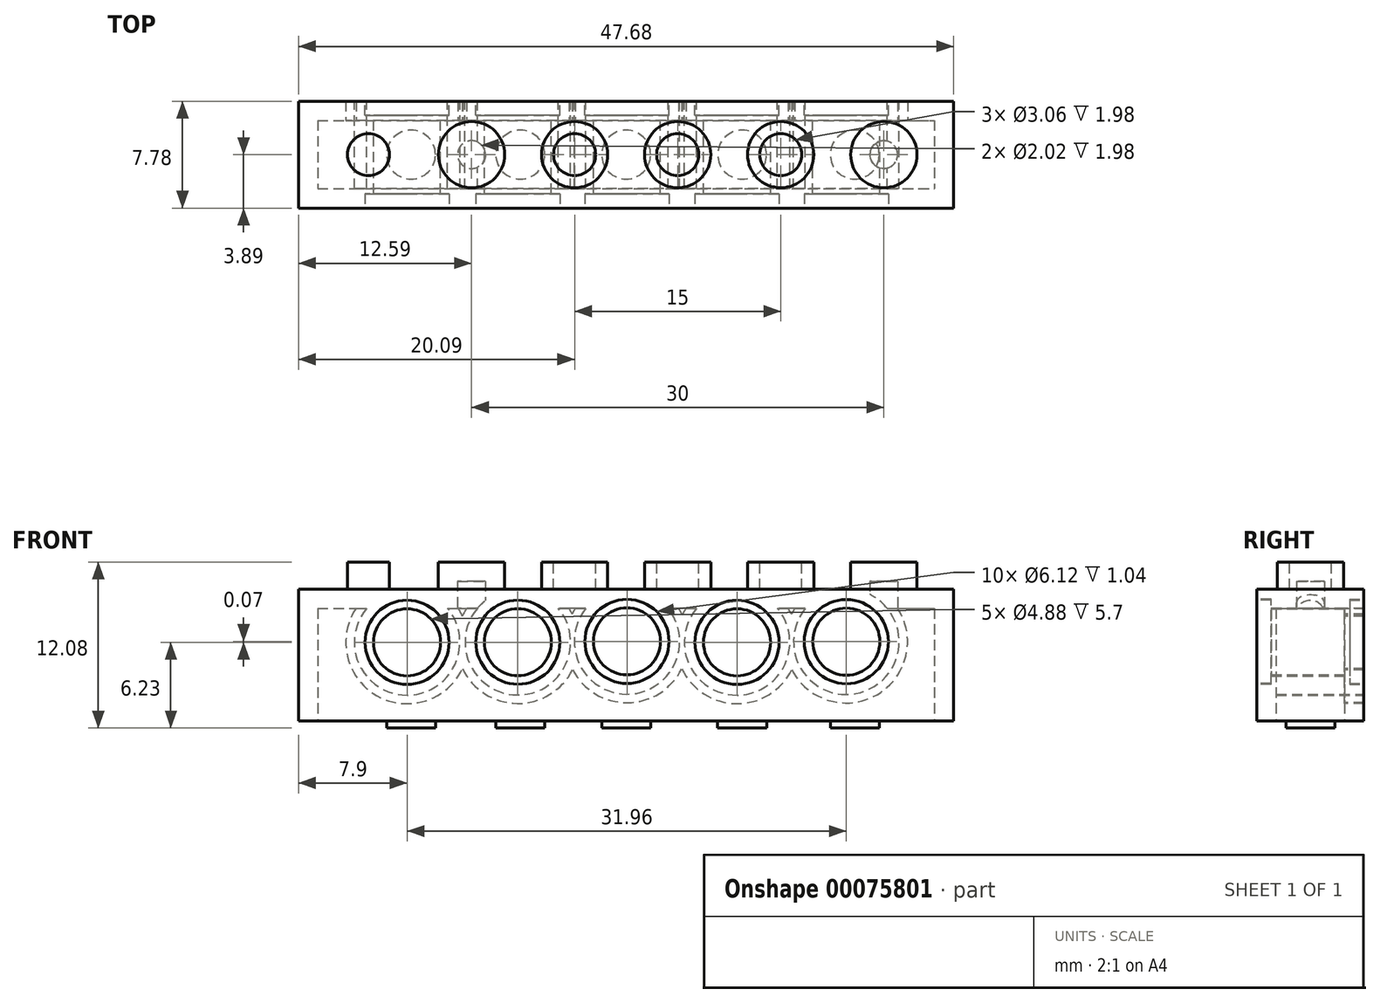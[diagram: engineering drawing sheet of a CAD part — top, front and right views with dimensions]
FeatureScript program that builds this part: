
annotation { "Feature Type Name" : "Feature", "Feature Type Description" : "" }
export const myFeature = defineFeature(function(context is Context, id is Id, definition is map)
    precondition{}
    {
        {
            var Q0;
            Q0=qCreatedBy(makeId("Top.planeOp"),FACE);
            var sketch = newSketch(context, id + "F0", { "sketchPlane" : qUnion([Q0])});
            skLineSegment(sketch, "E0.bottom", {"start": v(-23.84, 3.89) * mm, "end": v(23.84, 3.89) * mm});
            skLineSegment(sketch, "E0.top", {"start": v(-23.84, -3.89) * mm, "end": v(23.84, -3.89) * mm});
            skLineSegment(sketch, "E0.left", {"start": v(-23.84, 3.89) * mm, "end": v(-23.84, -3.89) * mm});
            skLineSegment(sketch, "E0.right", {"start": v(23.84, 3.89) * mm, "end": v(23.84, -3.89) * mm});
            skPoint(sketch, "E0.middle", {"position": v(0, 0) * mm});
            skSolve(sketch);
        }
        {
            var Q0;
            Q0=makeQuery(id+"F0.imprint","IMPRINT",FACE,{"disambiguationData":[TD([[makeQuery(id+"F0.imprint","IMPRINT",EDGE,{"derivedFrom":sQuery(id+"F0.wireOp",EDGE,"E0.bottom")}),-1.0]])]});
            extrude(context, id + "F1", {"entities" : qUnion([Q0]), "depth" : 9.6 * mm});
        }
        {
            var Q0;
            Q0=makeQuery(id+"F1.opExtrude","SWEPT_FACE",FACE,{"disambiguationData":[OSD([sQuery(id+"F0.wireOp",EDGE,"E0.bottom")])]});
            var sketch = newSketch(context, id + "F2", { "sketchPlane" : qUnion([Q0])});
            skLineSegment(sketch, "E1", {"start": v(-23.84, 4.8) * mm, "end": v(-18.45, 4.8) * mm});
            skLineSegment(sketch, "E2", {"start": v(-18.45, 9.6) * mm, "end": v(-18.45, 8.26) * mm});
            skLineSegment(sketch, "E3", {"start": v(-18.45, 0) * mm, "end": v(-18.45, 3.33) * mm});
            skCircle(sketch, "E4", {"center": v(-16.02, 5.78) * mm, "radius": 2.44 * mm});
            skPoint(sketch, "E4.first.point", {"position": v(-18.45, 5.83) * mm});
            skPoint(sketch, "E4.second.point", {"position": v(-13.58, 5.73) * mm});
            skPoint(sketch, "E4.third.point", {"position": v(-16.04, 3.34) * mm});
            skLineSegment(sketch, "E5", {"start": v(-13.58, 5.73) * mm, "end": v(-10.5, 5.73) * mm});
            skCircle(sketch, "E6", {"center": v(-8.07, 5.73) * mm, "radius": 2.44 * mm});
            skPoint(sketch, "E6.second.point", {"position": v(-5.63, 5.73) * mm});
            skPoint(sketch, "E6.third.point", {"position": v(-8.14, 8.17) * mm});
            skLineSegment(sketch, "E7", {"start": v(-5.57, 5.68) * mm, "end": v(-2.5, 5.68) * mm});
            skCircle(sketch, "E8", {"center": v(-0.06, 5.8) * mm, "radius": 2.44 * mm});
            skPoint(sketch, "E8.second.point", {"position": v(2.37, 5.68) * mm});
            skPoint(sketch, "E8.third.point", {"position": v(0, 8.24) * mm});
            skLineSegment(sketch, "E9", {"start": v(2.36, 5.74) * mm, "end": v(5.44, 5.74) * mm});
            skCircle(sketch, "E10", {"center": v(7.88, 5.74) * mm, "radius": 2.44 * mm});
            skPoint(sketch, "E10.second.point", {"position": v(10.31, 5.74) * mm});
            skPoint(sketch, "E10.third.point", {"position": v(7.78, 8.18) * mm});
            skLineSegment(sketch, "E11", {"start": v(10.43, 5.73) * mm, "end": v(13.5, 5.73) * mm});
            skCircle(sketch, "E12", {"center": v(15.94, 5.73) * mm, "radius": 2.44 * mm});
            skPoint(sketch, "E12.second.point", {"position": v(18.38, 5.73) * mm});
            skPoint(sketch, "E12.third.point", {"position": v(15.93, 8.17) * mm});
            skSolve(sketch);
        }
        {
            var Q0;
            Q0=makeQuery(id+"F2.imprint","IMPRINT",FACE,{"disambiguationData":[TD([[makeQuery(id+"F2.imprint","IMPRINT",EDGE,{"derivedFrom":sQuery(id+"F2.wireOp",EDGE,"E6")}),1.0]])]});
            var Q1;
            {var subQ0=sQuery(id+"F2.wireOp",EDGE,"E8");var subQ1=makeQuery(id+"F2.imprint","IMPRINT",VERTEX,{"disambiguationData":[OD(0.0)],"derivedFrom":subQ0});Q1=makeQuery(id+"F2.imprint","IMPRINT",FACE,{"disambiguationData":[TD([[makeQuery(id+"F2.imprint","IMPRINT",EDGE,{"disambiguationData":[TD([[subQ1,-1.0]])],"derivedFrom":subQ0}),1.0]])]});}
            var Q2;
            Q2=makeQuery(id+"F2.imprint","IMPRINT",FACE,{"disambiguationData":[TD([[makeQuery(id+"F2.imprint","IMPRINT",EDGE,{"derivedFrom":sQuery(id+"F2.wireOp",EDGE,"E10")}),1.0]])]});
            var Q3;
            Q3=makeQuery(id+"F2.imprint","IMPRINT",FACE,{"disambiguationData":[TD([[makeQuery(id+"F2.imprint","IMPRINT",EDGE,{"derivedFrom":sQuery(id+"F2.wireOp",EDGE,"E12")}),1.0]])]});
            var Q4;
            Q4=makeQuery(id+"F2.imprint","IMPRINT",FACE,{"disambiguationData":[TD([[makeQuery(id+"F2.imprint","IMPRINT",EDGE,{"derivedFrom":sQuery(id+"F2.wireOp",EDGE,"E4")}),1.0]])]});
            extrude(context, id + "F3", {"entities" : qUnion([Q0, Q1, Q2, Q3, Q4]), "operationType" : NewBodyOperationType.REMOVE, "oppositeDirection" : true, "depth" : 25.4 * mm});
        }
        {
            var Q0;
            Q0=makeQuery(id+"F1.opExtrude","CAP_FACE",FACE,{"disambiguationData":[OSD([sQuery(id+"F0.wireOp",EDGE,"E0.bottom"),sQuery(id+"F0.wireOp",EDGE,"E0.top"),sQuery(id+"F0.wireOp",EDGE,"E0.left"),sQuery(id+"F0.wireOp",EDGE,"E0.right")])],"isStart":false});
            var sketch = newSketch(context, id + "F4", { "sketchPlane" : qUnion([Q0])});
            skCircle(sketch, "E13", {"center": v(-18.75, 0) * mm, "radius": 2.41 * mm});
            skCircle(sketch, "E14", {"center": v(-11.25, 0) * mm, "radius": 2.41 * mm});
            skCircle(sketch, "E15", {"center": v(-3.75, 0) * mm, "radius": 2.41 * mm});
            skCircle(sketch, "E16", {"center": v(3.75, 0) * mm, "radius": 2.41 * mm});
            skCircle(sketch, "E17", {"center": v(11.25, 0) * mm, "radius": 2.41 * mm});
            skCircle(sketch, "E18", {"center": v(18.75, 0) * mm, "radius": 2.41 * mm});
            skSolve(sketch);
        }
        {
            var Q0;
            Q0=makeQuery(id+"F4.imprint","IMPRINT",FACE,{"disambiguationData":[TD([[makeQuery(id+"F4.imprint","IMPRINT",EDGE,{"derivedFrom":sQuery(id+"F4.wireOp",EDGE,"E14")}),1.0]])]});
            var Q1;
            Q1=makeQuery(id+"F4.imprint","IMPRINT",FACE,{"disambiguationData":[TD([[makeQuery(id+"F4.imprint","IMPRINT",EDGE,{"derivedFrom":sQuery(id+"F4.wireOp",EDGE,"E15")}),1.0]])]});
            var Q2;
            Q2=makeQuery(id+"F4.imprint","IMPRINT",FACE,{"disambiguationData":[TD([[makeQuery(id+"F4.imprint","IMPRINT",EDGE,{"derivedFrom":sQuery(id+"F4.wireOp",EDGE,"E16")}),1.0]])]});
            var Q3;
            Q3=makeQuery(id+"F4.imprint","IMPRINT",FACE,{"disambiguationData":[TD([[makeQuery(id+"F4.imprint","IMPRINT",EDGE,{"derivedFrom":sQuery(id+"F4.wireOp",EDGE,"E17")}),1.0]])]});
            var Q4;
            Q4=makeQuery(id+"F4.imprint","IMPRINT",FACE,{"disambiguationData":[TD([[makeQuery(id+"F4.imprint","IMPRINT",EDGE,{"derivedFrom":sQuery(id+"F4.wireOp",EDGE,"E18")}),1.0]])]});
            var Q5;
            Q5=makeQuery(id+"F4.imprint","IMPRINT",FACE,{"disambiguationData":[TD([[makeQuery(id+"F4.imprint","IMPRINT",EDGE,{"derivedFrom":sQuery(id+"F4.wireOp",EDGE,"E13")}),1.0]])]});
            extrude(context, id + "F5", {"entities" : qUnion([Q0, Q1, Q2, Q3, Q4, Q5]), "operationType" : NewBodyOperationType.ADD, "depth" : 1.98 * mm});
        }
        {
            var Q0;
            Q0=makeQuery(id+"F5.opExtrude","CAP_FACE",FACE,{"disambiguationData":[OSD([sQuery(id+"F4.wireOp",EDGE,"E13")])],"isStart":false});
            var sketch = newSketch(context, id + "F6", { "sketchPlane" : qUnion([Q0])});
            skLineSegment(sketch, "E19", {"start": v(-23.82, 0) * mm, "end": v(23.73, 0) * mm});
            skCircle(sketch, "E20", {"center": v(-18.75, 0) * mm, "radius": 1.52 * mm});
            skCircle(sketch, "E21", {"center": v(-11.25, 0) * mm, "radius": 1.52 * mm});
            skCircle(sketch, "E22", {"center": v(-3.75, 0) * mm, "radius": 1.53 * mm});
            skCircle(sketch, "E23", {"center": v(3.75, 0) * mm, "radius": 1.53 * mm});
            skCircle(sketch, "E24", {"center": v(11.25, 0) * mm, "radius": 1.53 * mm});
            skCircle(sketch, "E25", {"center": v(18.75, 0) * mm, "radius": 1.52 * mm});
            skLineSegment(sketch, "E26", {"start": v(-18.84, 1.52) * mm, "end": v(-18.84, 2.41) * mm});
            skLineSegment(sketch, "E27", {"start": v(-11.32, 1.52) * mm, "end": v(-11.32, 2.41) * mm});
            skLineSegment(sketch, "E28", {"start": v(-3.86, 1.52) * mm, "end": v(-3.86, 2.41) * mm});
            skLineSegment(sketch, "E29", {"start": v(3.89, 1.52) * mm, "end": v(3.89, 2.41) * mm});
            skLineSegment(sketch, "E30", {"start": v(11.16, 1.52) * mm, "end": v(11.16, 2.41) * mm});
            skLineSegment(sketch, "E31", {"start": v(18.83, 1.52) * mm, "end": v(18.83, 2.41) * mm});
            skSolve(sketch);
        }
        {
            var Q0;
            {var subQ0=sQuery(id+"F6.wireOp",EDGE,"E20");var subQ1=sQuery(id+"F6.wireOp",EDGE,"E19");var subQ2=makeQuery(id+"F6.imprint","INTERSECT",VERTEX,{"disambiguationData":[OD(0.0)],"derivedFrom":[subQ1,subQ0]});Q0=makeQuery(id+"F6.imprint","IMPRINT",FACE,{"disambiguationData":[TD([[makeQuery(id+"F6.imprint","IMPRINT",EDGE,{"disambiguationData":[TD([[subQ2,-1.0]])],"derivedFrom":subQ1}),1.0]])]});}
            var Q1;
            {var subQ0=sQuery(id+"F6.wireOp",EDGE,"E20");var subQ1=sQuery(id+"F6.wireOp",EDGE,"E19");var subQ2=makeQuery(id+"F6.imprint","INTERSECT",VERTEX,{"disambiguationData":[OD(0.0)],"derivedFrom":[subQ1,subQ0]});Q1=makeQuery(id+"F6.imprint","IMPRINT",FACE,{"disambiguationData":[TD([[makeQuery(id+"F6.imprint","IMPRINT",EDGE,{"disambiguationData":[TD([[subQ2,-1.0]])],"derivedFrom":subQ1}),-1.0]])]});}
            var Q2;
            {var subQ0=sQuery(id+"F6.wireOp",EDGE,"E21");var subQ1=sQuery(id+"F6.wireOp",EDGE,"E19");var subQ2=makeQuery(id+"F6.imprint","INTERSECT",VERTEX,{"disambiguationData":[OD(0.0)],"derivedFrom":[subQ1,subQ0]});Q2=makeQuery(id+"F6.imprint","IMPRINT",FACE,{"disambiguationData":[TD([[makeQuery(id+"F6.imprint","IMPRINT",EDGE,{"disambiguationData":[TD([[subQ2,1.0]])],"derivedFrom":subQ1}),-1.0]])]});}
            var Q3;
            {var subQ0=sQuery(id+"F6.wireOp",EDGE,"E21");var subQ4=makeQuery(id+"F6.imprint","IMPRINT",VERTEX,{"derivedFrom":subQ0});Q3=makeQuery(id+"F6.imprint","IMPRINT",FACE,{"disambiguationData":[TD([[makeQuery(id+"F6.imprint","IMPRINT",EDGE,{"disambiguationData":[TD([[subQ4,1.0]])],"derivedFrom":subQ0}),1.0]])]});}
            var Q4;
            {var subQ0=sQuery(id+"F6.wireOp",EDGE,"E22");var subQ4=makeQuery(id+"F6.imprint","IMPRINT",VERTEX,{"derivedFrom":subQ0});Q4=makeQuery(id+"F6.imprint","IMPRINT",FACE,{"disambiguationData":[TD([[makeQuery(id+"F6.imprint","IMPRINT",EDGE,{"disambiguationData":[TD([[subQ4,1.0]])],"derivedFrom":subQ0}),1.0]])]});}
            var Q5;
            {var subQ0=sQuery(id+"F6.wireOp",EDGE,"E22");var subQ1=sQuery(id+"F6.wireOp",EDGE,"E19");var subQ2=makeQuery(id+"F6.imprint","INTERSECT",VERTEX,{"disambiguationData":[OD(0.0)],"derivedFrom":[subQ1,subQ0]});Q5=makeQuery(id+"F6.imprint","IMPRINT",FACE,{"disambiguationData":[TD([[makeQuery(id+"F6.imprint","IMPRINT",EDGE,{"disambiguationData":[TD([[subQ2,1.0]])],"derivedFrom":subQ1}),-1.0]])]});}
            var Q6;
            {var subQ0=sQuery(id+"F6.wireOp",EDGE,"E23");var subQ4=makeQuery(id+"F6.imprint","IMPRINT",VERTEX,{"derivedFrom":subQ0});Q6=makeQuery(id+"F6.imprint","IMPRINT",FACE,{"disambiguationData":[TD([[makeQuery(id+"F6.imprint","IMPRINT",EDGE,{"disambiguationData":[TD([[subQ4,1.0]])],"derivedFrom":subQ0}),1.0]])]});}
            var Q7;
            {var subQ0=sQuery(id+"F6.wireOp",EDGE,"E23");var subQ1=sQuery(id+"F6.wireOp",EDGE,"E19");var subQ2=makeQuery(id+"F6.imprint","INTERSECT",VERTEX,{"disambiguationData":[OD(0.0)],"derivedFrom":[subQ1,subQ0]});Q7=makeQuery(id+"F6.imprint","IMPRINT",FACE,{"disambiguationData":[TD([[makeQuery(id+"F6.imprint","IMPRINT",EDGE,{"disambiguationData":[TD([[subQ2,1.0]])],"derivedFrom":subQ1}),-1.0]])]});}
            var Q8;
            {var subQ0=sQuery(id+"F6.wireOp",EDGE,"E24");var subQ4=makeQuery(id+"F6.imprint","IMPRINT",VERTEX,{"derivedFrom":subQ0});Q8=makeQuery(id+"F6.imprint","IMPRINT",FACE,{"disambiguationData":[TD([[makeQuery(id+"F6.imprint","IMPRINT",EDGE,{"disambiguationData":[TD([[subQ4,1.0]])],"derivedFrom":subQ0}),1.0]])]});}
            var Q9;
            {var subQ0=sQuery(id+"F6.wireOp",EDGE,"E24");var subQ1=sQuery(id+"F6.wireOp",EDGE,"E19");var subQ2=makeQuery(id+"F6.imprint","INTERSECT",VERTEX,{"disambiguationData":[OD(0.0)],"derivedFrom":[subQ1,subQ0]});Q9=makeQuery(id+"F6.imprint","IMPRINT",FACE,{"disambiguationData":[TD([[makeQuery(id+"F6.imprint","IMPRINT",EDGE,{"disambiguationData":[TD([[subQ2,1.0]])],"derivedFrom":subQ1}),-1.0]])]});}
            var Q10;
            {var subQ0=sQuery(id+"F6.wireOp",EDGE,"E25");var subQ4=makeQuery(id+"F6.imprint","IMPRINT",VERTEX,{"derivedFrom":subQ0});Q10=makeQuery(id+"F6.imprint","IMPRINT",FACE,{"disambiguationData":[TD([[makeQuery(id+"F6.imprint","IMPRINT",EDGE,{"disambiguationData":[TD([[subQ4,1.0]])],"derivedFrom":subQ0}),1.0]])]});}
            var Q11;
            {var subQ0=sQuery(id+"F6.wireOp",EDGE,"E25");var subQ1=sQuery(id+"F6.wireOp",EDGE,"E19");var subQ2=makeQuery(id+"F6.imprint","INTERSECT",VERTEX,{"disambiguationData":[OD(0.0)],"derivedFrom":[subQ1,subQ0]});Q11=makeQuery(id+"F6.imprint","IMPRINT",FACE,{"disambiguationData":[TD([[makeQuery(id+"F6.imprint","IMPRINT",EDGE,{"disambiguationData":[TD([[subQ2,1.0]])],"derivedFrom":subQ1}),-1.0]])]});}
            extrude(context, id + "F7", {"entities" : qUnion([Q0, Q1, Q2, Q3, Q4, Q5, Q6, Q7, Q8, Q9, Q10, Q11]), "operationType" : NewBodyOperationType.REMOVE, "oppositeDirection" : true, "depth" : 1.98 * mm});
        }
        {
            var Q0;
            Q0=makeQuery(id+"F1.opExtrude","SWEPT_FACE",FACE,{"disambiguationData":[OSD([sQuery(id+"F0.wireOp",EDGE,"E0.top")])]});
            var sketch = newSketch(context, id + "F8", { "sketchPlane" : qUnion([Q0])});
            skCircle(sketch, "E32", {"center": v(-15.94, 5.73) * mm, "radius": 3.06 * mm});
            skCircle(sketch, "E33", {"center": v(-7.88, 5.74) * mm, "radius": 3.06 * mm});
            skCircle(sketch, "E34", {"center": v(0.06, 5.8) * mm, "radius": 3.06 * mm});
            skCircle(sketch, "E35", {"center": v(8.07, 5.73) * mm, "radius": 3.06 * mm});
            skCircle(sketch, "E36", {"center": v(16.02, 5.78) * mm, "radius": 3.06 * mm});
            skSolve(sketch);
        }
        {
            var Q0;
            Q0=makeQuery(id+"F8.imprint","IMPRINT",FACE,{"disambiguationData":[TD([[makeQuery(id+"F8.imprint","IMPRINT",EDGE,{"derivedFrom":sQuery(id+"F8.wireOp",EDGE,"E32")}),1.0]])]});
            var Q1;
            Q1=makeQuery(id+"F8.imprint","IMPRINT",FACE,{"disambiguationData":[TD([[makeQuery(id+"F8.imprint","IMPRINT",EDGE,{"derivedFrom":sQuery(id+"F8.wireOp",EDGE,"E33")}),1.0]])]});
            var Q2;
            Q2=makeQuery(id+"F8.imprint","IMPRINT",FACE,{"disambiguationData":[TD([[makeQuery(id+"F8.imprint","IMPRINT",EDGE,{"derivedFrom":sQuery(id+"F8.wireOp",EDGE,"E34")}),1.0]])]});
            var Q3;
            Q3=makeQuery(id+"F8.imprint","IMPRINT",FACE,{"disambiguationData":[TD([[makeQuery(id+"F8.imprint","IMPRINT",EDGE,{"derivedFrom":sQuery(id+"F8.wireOp",EDGE,"E35")}),1.0]])]});
            var Q4;
            Q4=makeQuery(id+"F8.imprint","IMPRINT",FACE,{"disambiguationData":[TD([[makeQuery(id+"F8.imprint","IMPRINT",EDGE,{"derivedFrom":sQuery(id+"F8.wireOp",EDGE,"E36")}),1.0]])]});
            extrude(context, id + "F9", {"entities" : qUnion([Q0, Q1, Q2, Q3, Q4]), "operationType" : NewBodyOperationType.REMOVE, "oppositeDirection" : true, "depth" : 1.04 * mm});
        }
        {
            var Q0;
            Q0=makeQuery(id+"F1.opExtrude","SWEPT_FACE",FACE,{"disambiguationData":[OSD([sQuery(id+"F0.wireOp",EDGE,"E0.bottom")])]});
            var sketch = newSketch(context, id + "F10", { "sketchPlane" : qUnion([Q0])});
            skCircle(sketch, "E37", {"center": v(-16.02, 5.78) * mm, "radius": 3.06 * mm});
            skCircle(sketch, "E38", {"center": v(-8.07, 5.73) * mm, "radius": 3.06 * mm});
            skCircle(sketch, "E39", {"center": v(-0.06, 5.8) * mm, "radius": 3.06 * mm});
            skCircle(sketch, "E40", {"center": v(7.88, 5.74) * mm, "radius": 3.06 * mm});
            skCircle(sketch, "E41", {"center": v(15.94, 5.73) * mm, "radius": 3.06 * mm});
            skSolve(sketch);
        }
        {
            var Q0;
            Q0=makeQuery(id+"F10.imprint","IMPRINT",FACE,{"disambiguationData":[TD([[makeQuery(id+"F10.imprint","IMPRINT",EDGE,{"derivedFrom":sQuery(id+"F10.wireOp",EDGE,"E37")}),1.0]])]});
            var Q1;
            Q1=makeQuery(id+"F10.imprint","IMPRINT",FACE,{"disambiguationData":[TD([[makeQuery(id+"F10.imprint","IMPRINT",EDGE,{"derivedFrom":sQuery(id+"F10.wireOp",EDGE,"E38")}),1.0]])]});
            var Q2;
            Q2=makeQuery(id+"F10.imprint","IMPRINT",FACE,{"disambiguationData":[TD([[makeQuery(id+"F10.imprint","IMPRINT",EDGE,{"derivedFrom":sQuery(id+"F10.wireOp",EDGE,"E39")}),1.0]])]});
            var Q3;
            Q3=makeQuery(id+"F10.imprint","IMPRINT",FACE,{"disambiguationData":[TD([[makeQuery(id+"F10.imprint","IMPRINT",EDGE,{"derivedFrom":sQuery(id+"F10.wireOp",EDGE,"E40")}),1.0]])]});
            var Q4;
            Q4=makeQuery(id+"F10.imprint","IMPRINT",FACE,{"disambiguationData":[TD([[makeQuery(id+"F10.imprint","IMPRINT",EDGE,{"derivedFrom":sQuery(id+"F10.wireOp",EDGE,"E41")}),1.0]])]});
            extrude(context, id + "F11", {"entities" : qUnion([Q0, Q1, Q2, Q3, Q4]), "operationType" : NewBodyOperationType.REMOVE, "oppositeDirection" : true, "depth" : 1.04 * mm});
        }
        {
            var Q0;
            Q0=makeQuery(id+"F1.opExtrude","CAP_FACE",FACE,{"disambiguationData":[OSD([sQuery(id+"F0.wireOp",EDGE,"E0.bottom"),sQuery(id+"F0.wireOp",EDGE,"E0.top"),sQuery(id+"F0.wireOp",EDGE,"E0.left"),sQuery(id+"F0.wireOp",EDGE,"E0.right")])],"isStart":true});
            var Q1;
            Q1=makeQuery(id+"F1.opExtrude","SWEPT_BODY",BODY,{"disambiguationData":[OSD([sQuery(id+"F0.wireOp",EDGE,"E0.bottom"),sQuery(id+"F0.wireOp",EDGE,"E0.top"),sQuery(id+"F0.wireOp",EDGE,"E0.left"),sQuery(id+"F0.wireOp",EDGE,"E0.right")])]});
            shell(context, id + "F12", {"entities" : qUnion([Q0]), "parts" : qUnion([Q1]), "thickness" : 1.4 * mm});
        }
        {
            var Q0;
            Q0=makeQuery(id+"F12.opShell","OFFSET_FACE",FACE,{"disambiguationData":[OSD([sQuery(id+"F2.wireOp",EDGE,"E4"),sQuery(id+"F2.wireOp",EDGE,"E6"),sQuery(id+"F2.wireOp",EDGE,"E8"),sQuery(id+"F2.wireOp",EDGE,"E10"),sQuery(id+"F2.wireOp",EDGE,"E12"),sQuery(id+"F10.wireOp",EDGE,"E37"),sQuery(id+"F10.wireOp",EDGE,"E38"),sQuery(id+"F10.wireOp",EDGE,"E39"),sQuery(id+"F10.wireOp",EDGE,"E40"),sQuery(id+"F10.wireOp",EDGE,"E41")])]});
            extrude(context, id + "F13", {"entities" : qUnion([Q0]), "operationType" : NewBodyOperationType.REMOVE, "oppositeDirection" : true, "depth" : 25.4 * mm});
        }
        {
            var Q0;
            Q0=makeQuery(id+"F12.opShell","OFFSET_FACE",FACE,{"disambiguationData":[OSD([sQuery(id+"F0.wireOp",EDGE,"E0.top"),sQuery(id+"F2.wireOp",EDGE,"E4"),sQuery(id+"F2.wireOp",EDGE,"E6"),sQuery(id+"F2.wireOp",EDGE,"E8"),sQuery(id+"F2.wireOp",EDGE,"E10"),sQuery(id+"F2.wireOp",EDGE,"E12"),sQuery(id+"F8.wireOp",EDGE,"E32"),sQuery(id+"F8.wireOp",EDGE,"E33"),sQuery(id+"F8.wireOp",EDGE,"E34"),sQuery(id+"F8.wireOp",EDGE,"E35"),sQuery(id+"F8.wireOp",EDGE,"E36")])]});
            var Q1;
            Q1=makeQuery(id+"F12.opShell","OFFSET_FACE",FACE,{"disambiguationData":[OSD([sQuery(id+"F0.wireOp",EDGE,"E0.top")]),OD(4.0)]});
            extrude(context, id + "F14", {"entities" : qUnion([Q0]), "operationType" : NewBodyOperationType.REMOVE, "endBound" : BoundingType.UP_TO_SURFACE, "oppositeDirection" : true, "endBoundEntityFace" : qUnion([Q1]), "depth" : 25.4 * mm});
        }
        {
            var Q0;
            Q0=makeQuery(id+"F1.opExtrude","CAP_FACE",FACE,{"disambiguationData":[OSD([sQuery(id+"F0.wireOp",EDGE,"E0.bottom"),sQuery(id+"F0.wireOp",EDGE,"E0.top"),sQuery(id+"F0.wireOp",EDGE,"E0.left"),sQuery(id+"F0.wireOp",EDGE,"E0.right")])],"isStart":true});
            var sketch = newSketch(context, id + "F15", { "sketchPlane" : qUnion([Q0])});
            skCircle(sketch, "E42", {"center": v(0, 0) * mm, "radius": 1.78 * mm});
            skCircle(sketch, "E43", {"center": v(-7.7, 0) * mm, "radius": 1.78 * mm});
            skCircle(sketch, "E44", {"center": v(-15.65, 0) * mm, "radius": 1.78 * mm});
            skCircle(sketch, "E45", {"center": v(8.44, 0) * mm, "radius": 1.78 * mm});
            skCircle(sketch, "E46", {"center": v(16.64, 0) * mm, "radius": 1.78 * mm});
            skLineSegment(sketch, "E47", {"start": v(-1.78, 0) * mm, "end": v(-5.93, 0) * mm});
            skLineSegment(sketch, "E48", {"start": v(1.78, 0) * mm, "end": v(6.66, 0) * mm});
            skLineSegment(sketch, "E49", {"start": v(-9.49, 0) * mm, "end": v(-13.87, 0) * mm});
            skLineSegment(sketch, "E50", {"start": v(10.22, 0) * mm, "end": v(14.87, 0) * mm});
            skSolve(sketch);
        }
        {
            var Q0;
            Q0=makeQuery(id+"F15.imprint","IMPRINT",FACE,{"disambiguationData":[TD([[makeQuery(id+"F15.imprint","IMPRINT",EDGE,{"derivedFrom":sQuery(id+"F15.wireOp",EDGE,"E44")}),1.0]])]});
            var Q1;
            {var subQ0=sQuery(id+"F15.wireOp",EDGE,"E43");var subQ1=makeQuery(id+"F15.imprint","IMPRINT",VERTEX,{"disambiguationData":[OD(0.0)],"derivedFrom":subQ0});Q1=makeQuery(id+"F15.imprint","IMPRINT",FACE,{"disambiguationData":[TD([[makeQuery(id+"F15.imprint","IMPRINT",EDGE,{"disambiguationData":[TD([[subQ1,-1.0]])],"derivedFrom":subQ0}),1.0]])]});}
            var Q2;
            {var subQ0=sQuery(id+"F15.wireOp",EDGE,"E42");var subQ1=makeQuery(id+"F15.imprint","IMPRINT",VERTEX,{"disambiguationData":[OD(0.0)],"derivedFrom":subQ0});Q2=makeQuery(id+"F15.imprint","IMPRINT",FACE,{"disambiguationData":[TD([[makeQuery(id+"F15.imprint","IMPRINT",EDGE,{"disambiguationData":[TD([[subQ1,1.0]])],"derivedFrom":subQ0}),1.0]])]});}
            var Q3;
            {var subQ0=sQuery(id+"F15.wireOp",EDGE,"E45");var subQ1=makeQuery(id+"F15.imprint","IMPRINT",VERTEX,{"disambiguationData":[OD(0.0)],"derivedFrom":subQ0});Q3=makeQuery(id+"F15.imprint","IMPRINT",FACE,{"disambiguationData":[TD([[makeQuery(id+"F15.imprint","IMPRINT",EDGE,{"disambiguationData":[TD([[subQ1,1.0]])],"derivedFrom":subQ0}),1.0]])]});}
            var Q4;
            Q4=makeQuery(id+"F15.imprint","IMPRINT",FACE,{"disambiguationData":[TD([[makeQuery(id+"F15.imprint","IMPRINT",EDGE,{"derivedFrom":sQuery(id+"F15.wireOp",EDGE,"E46")}),1.0]])]});
            extrude(context, id + "F16", {"entities" : qUnion([Q0, Q1, Q2, Q3, Q4]), "depth" : 0.5 * mm});
        }
    });
